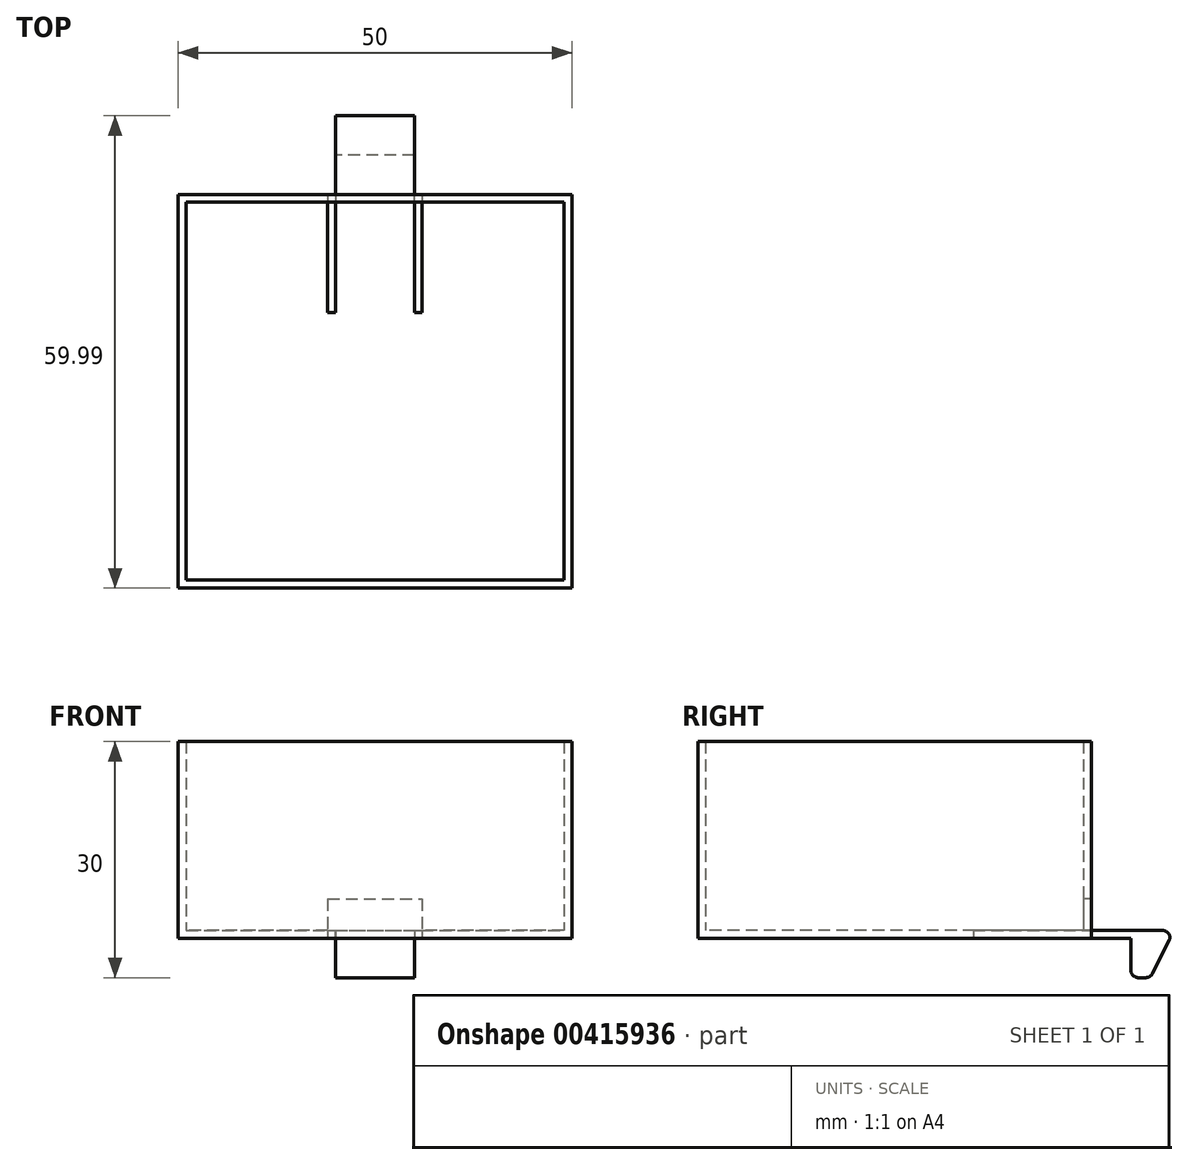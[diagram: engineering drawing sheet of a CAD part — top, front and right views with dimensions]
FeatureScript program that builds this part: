
annotation { "Feature Type Name" : "Feature", "Feature Type Description" : "" }
export const myFeature = defineFeature(function(context is Context, id is Id, definition is map)
    precondition{}
    {
        {
            var Q0;
            Q0=qCreatedBy(makeId("Top.planeOp"),FACE);
            var sketch = newSketch(context, id + "F0", { "sketchPlane" : qUnion([Q0])});
            skLineSegment(sketch, "E0.bottom", {"start": v(0, 0) * mm, "end": v(50, 0) * mm});
            skLineSegment(sketch, "E0.left", {"start": v(0, 0) * mm, "end": v(0, 50) * mm});
            skLineSegment(sketch, "E0.right", {"start": v(50, 0) * mm, "end": v(50, 50) * mm});
            skLineSegment(sketch, "E1.top", {"start": v(19, 35) * mm, "end": v(20, 35) * mm});
            skLineSegment(sketch, "E1.left", {"start": v(19, 50) * mm, "end": v(19, 35) * mm});
            skLineSegment(sketch, "E2.top", {"start": v(30, 35) * mm, "end": v(31, 35) * mm});
            skLineSegment(sketch, "E2.right", {"start": v(31, 50) * mm, "end": v(31, 35) * mm});
            skLineSegment(sketch, "E3", {"start": v(20, 60) * mm, "end": v(30, 60) * mm});
            skLineSegment(sketch, "E4", {"start": v(0, 50) * mm, "end": v(19, 50) * mm});
            skLineSegment(sketch, "E5", {"start": v(31, 50) * mm, "end": v(50, 50) * mm});
            skLineSegment(sketch, "E6", {"start": v(20, 60) * mm, "end": v(20, 35) * mm});
            skLineSegment(sketch, "E7", {"start": v(30, 35) * mm, "end": v(30, 60) * mm});
            skSolve(sketch);
        }
        {
            var Q0;
            Q0 = qSketchRegion(id + "F0", true);
            extrude(context, id + "F1", {"entities" : qUnion([Q0]), "depth" : 1 * mm});
        }
        {
            var Q0;
            Q0=qCreatedBy(makeId("Top.planeOp"),FACE);
            var sketch = newSketch(context, id + "F2", { "sketchPlane" : qUnion([Q0])});
            skLineSegment(sketch, "E8", {"start": v(0, 0) * mm, "end": v(50, 0) * mm});
            skLineSegment(sketch, "E9", {"start": v(50, 0) * mm, "end": v(50, 50) * mm});
            skLineSegment(sketch, "E10", {"start": v(50, 50) * mm, "end": v(31, 50) * mm});
            skLineSegment(sketch, "E11", {"start": v(31, 50) * mm, "end": v(31, 49) * mm});
            skLineSegment(sketch, "E12", {"start": v(31, 49) * mm, "end": v(49, 49) * mm});
            skLineSegment(sketch, "E13", {"start": v(49, 49) * mm, "end": v(49, 1) * mm});
            skLineSegment(sketch, "E14", {"start": v(49, 1) * mm, "end": v(1, 1) * mm});
            skLineSegment(sketch, "E15", {"start": v(1, 1) * mm, "end": v(1, 49) * mm});
            skLineSegment(sketch, "E16", {"start": v(1, 49) * mm, "end": v(19, 49) * mm});
            skLineSegment(sketch, "E17", {"start": v(19, 49) * mm, "end": v(19, 50) * mm});
            skLineSegment(sketch, "E18", {"start": v(19, 50) * mm, "end": v(0, 50) * mm});
            skLineSegment(sketch, "E19", {"start": v(0, 50) * mm, "end": v(0, 0) * mm});
            skSolve(sketch);
        }
        {
            var Q0;
            Q0 = qSketchRegion(id + "F2", true);
            extrude(context, id + "F3", {"entities" : qUnion([Q0]), "operationType" : NewBodyOperationType.ADD, "depth" : 25 * mm});
        }
        {
            var Q0;
            Q0=qCreatedBy(makeId("Right.planeOp"),FACE);
            cPlane(context, id + "F4", {"entities" : qUnion([Q0]), "cplaneType" : CPlaneType.OFFSET, "offset" : 25 * mm, "width" : 150 * mm, "height" : 150 * mm});
        }
        {
            var Q0;
            Q0=qCreatedBy(id+"F4.planeOp",FACE);
            var sketch = newSketch(context, id + "F5", { "sketchPlane" : qUnion([Q0])});
            skLineSegment(sketch, "E20", {"start": v(60, 0) * mm, "end": v(57.5, -5) * mm});
            skLineSegment(sketch, "E21", {"start": v(57.5, -5) * mm, "end": v(55, -5) * mm});
            skLineSegment(sketch, "E22", {"start": v(55, -5) * mm, "end": v(55, 0) * mm});
            skLineSegment(sketch, "E23", {"start": v(55, 0) * mm, "end": v(60, 0) * mm});
            skSolve(sketch);
        }
        {
            var Q0;
            Q0 = qSketchRegion(id + "F5", true);
            extrude(context, id + "F6", {"entities" : qUnion([Q0]), "operationType" : NewBodyOperationType.ADD, "depth" : 5 * mm, "hasSecondDirection" : true, "secondDirectionOppositeDirection" : true, "secondDirectionDepth" : 5 * mm});
        }
        {
            var Q0;
            Q0=qCreatedBy(makeId("Top.planeOp"),FACE);
            cPlane(context, id + "F7", {"entities" : qUnion([Q0]), "cplaneType" : CPlaneType.OFFSET, "offset" : 25 * mm, "width" : 150 * mm, "height" : 150 * mm});
        }
        {
            var Q0;
            Q0=qCreatedBy(id+"F7.planeOp",FACE);
            var sketch = newSketch(context, id + "F8", { "sketchPlane" : qUnion([Q0])});
            skLineSegment(sketch, "E24.bottom", {"start": v(19, 50) * mm, "end": v(31, 50) * mm});
            skLineSegment(sketch, "E24.top", {"start": v(19, 49) * mm, "end": v(31, 49) * mm});
            skLineSegment(sketch, "E24.left", {"start": v(19, 50) * mm, "end": v(19, 49) * mm});
            skLineSegment(sketch, "E24.right", {"start": v(31, 50) * mm, "end": v(31, 49) * mm});
            skSolve(sketch);
        }
        {
            var Q0;
            Q0 = qSketchRegion(id + "F8", true);
            extrude(context, id + "F9", {"entities" : qUnion([Q0]), "operationType" : NewBodyOperationType.ADD, "oppositeDirection" : true, "depth" : 20 * mm});
        }
        {
            var Q0;
            Q0=makeQuery(id+"F6.opExtrude","SWEPT_EDGE",EDGE,{"disambiguationData":[OSD([sQuery(id+"F5.wireOp",EDGE,"E20"),sQuery(id+"F5.wireOp",EDGE,"E21")])]});
            var Q1;
            Q1=makeQuery(id+"F6.opExtrude","SWEPT_EDGE",EDGE,{"disambiguationData":[OSD([sQuery(id+"F5.wireOp",EDGE,"E21"),sQuery(id+"F5.wireOp",EDGE,"E22")])]});
            var Q2;
            Q2=makeQuery(id+"F6.boolean.opBoolean","MERGE",EDGE,{"derivedFrom":[makeQuery(id+"F1.opExtrude","CAP_EDGE",EDGE,{"disambiguationData":[OSD([sQuery(id+"F0.wireOp",EDGE,"E3")])],"isStart":true}),makeQuery(id+"F6.opExtrude","SWEPT_EDGE",EDGE,{"disambiguationData":[OSD([sQuery(id+"F5.wireOp",EDGE,"E20"),sQuery(id+"F5.wireOp",EDGE,"E23")])]})]});
            var Q3;
            Q3=makeQuery(id+"F1.opExtrude","CAP_EDGE",EDGE,{"disambiguationData":[OSD([sQuery(id+"F0.wireOp",EDGE,"E3")])],"isStart":false});
            fillet(context, id + "F10", {"entities" : qUnion([Q0, Q1, Q2, Q3]), "radius" : 1 * mm, "tangentPropagation" : true, "allowEdgeOverflow" : false});
        }
    });
